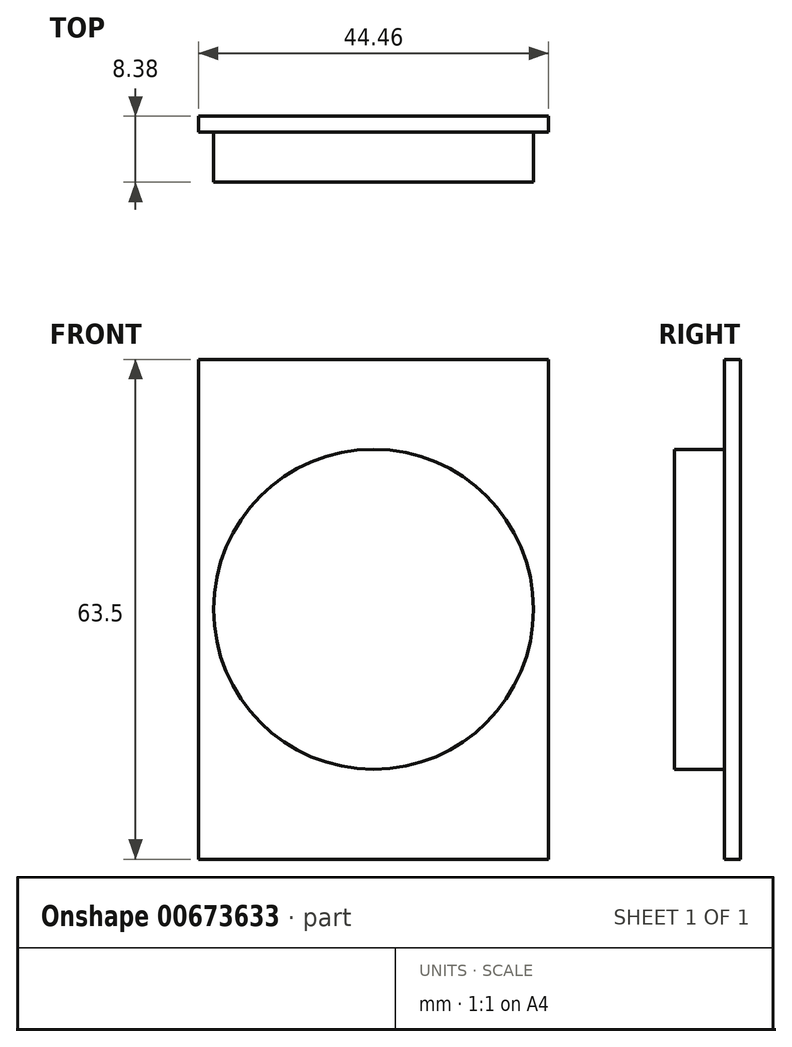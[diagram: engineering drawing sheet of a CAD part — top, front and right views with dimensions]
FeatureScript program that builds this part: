
annotation { "Feature Type Name" : "Feature", "Feature Type Description" : "" }
export const myFeature = defineFeature(function(context is Context, id is Id, definition is map)
    precondition{}
    {
        {
            var Q0;
            Q0=qCreatedBy(makeId("Front.planeOp"),FACE);
            var sketch = newSketch(context, id + "F0", { "sketchPlane" : qUnion([Q0])});
            skLineSegment(sketch, "E0.bottom", {"start": v(22.23, 31.75) * mm, "end": v(-22.23, 31.75) * mm});
            skLineSegment(sketch, "E0.top", {"start": v(22.23, -31.75) * mm, "end": v(-22.23, -31.75) * mm});
            skLineSegment(sketch, "E0.left", {"start": v(22.23, 31.75) * mm, "end": v(22.23, -31.75) * mm});
            skLineSegment(sketch, "E0.right", {"start": v(-22.23, 31.75) * mm, "end": v(-22.23, -31.75) * mm});
            skPoint(sketch, "E0.middle", {"position": v(0, 0) * mm});
            skSolve(sketch);
        }
        {
            var Q0;
            Q0=qSketchRegion(id+"F0",true);
            extrude(context, id + "F1", {"entities" : qUnion([Q0]), "depth" : 2.03 * mm, "offsetDistance" : 25.4 * mm});
        }
        {
            var Q0;
            Q0=makeQuery(id+"F1.opExtrude","CAP_FACE",FACE,{"disambiguationData":[OSD([sQuery(id+"F0.wireOp",EDGE,"E0.bottom"),sQuery(id+"F0.wireOp",EDGE,"E0.top"),sQuery(id+"F0.wireOp",EDGE,"E0.left"),sQuery(id+"F0.wireOp",EDGE,"E0.right")])],"isStart":false});
            var sketch = newSketch(context, id + "F2", { "sketchPlane" : qUnion([Q0])});
            skCircle(sketch, "E1", {"center": v(0, 0) * mm, "radius": 20.32 * mm});
            skSolve(sketch);
        }
        {
            var Q0;
            Q0=qSketchRegion(id+"F2",true);
            extrude(context, id + "F3", {"entities" : qUnion([Q0]), "operationType" : NewBodyOperationType.ADD, "depth" : 6.35 * mm, "offsetDistance" : 25.4 * mm});
        }
    });
